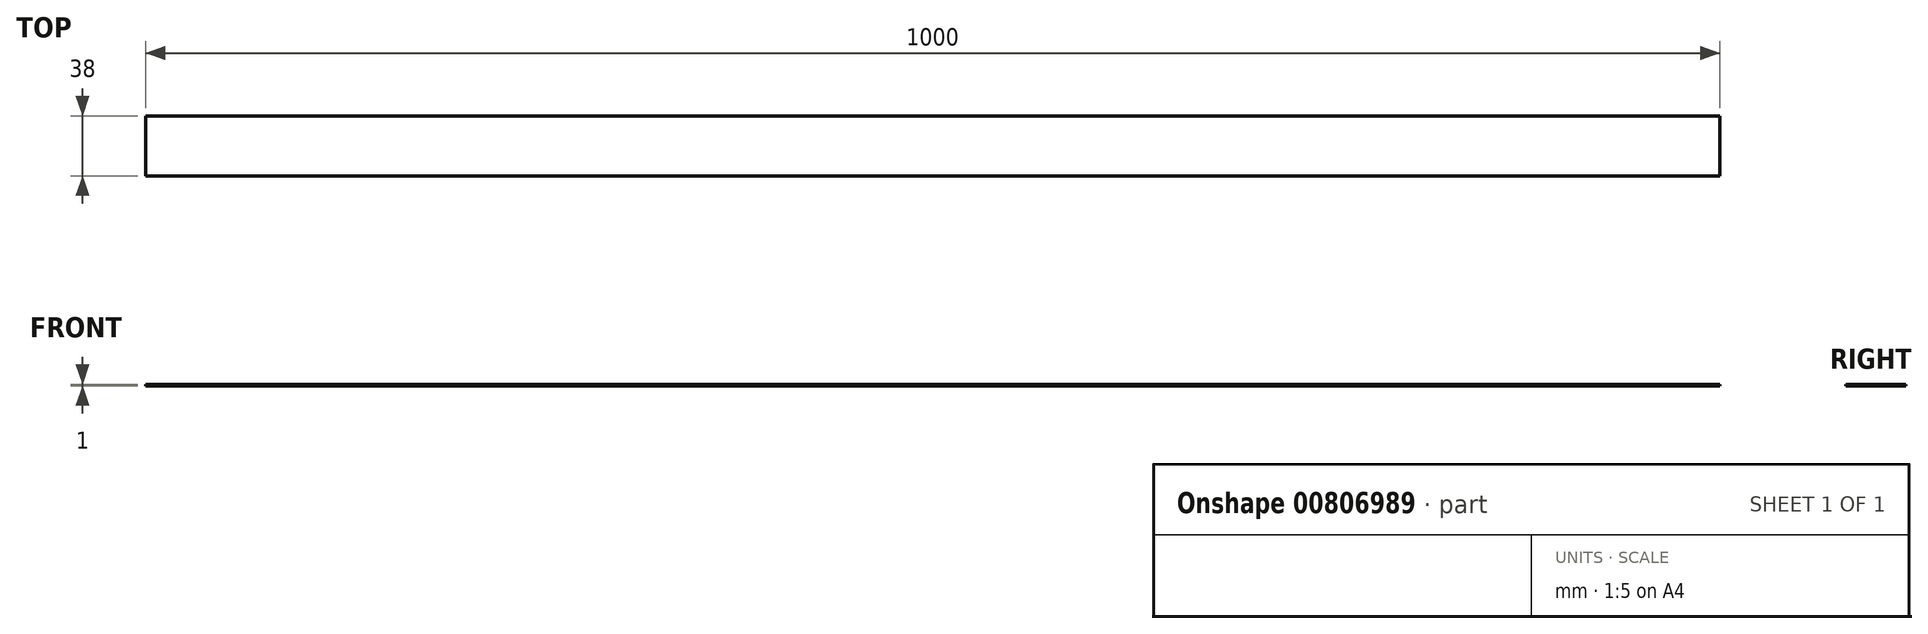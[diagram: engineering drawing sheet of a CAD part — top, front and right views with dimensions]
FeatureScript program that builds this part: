
annotation { "Feature Type Name" : "Feature", "Feature Type Description" : "" }
export const myFeature = defineFeature(function(context is Context, id is Id, definition is map)
    precondition{}
    {
        {
            var Q0;
            Q0=qCreatedBy(makeId("Top.planeOp"),FACE);
            var sketch = newSketch(context, id + "F0", { "sketchPlane" : qUnion([Q0])});
            skLineSegment(sketch, "E0.bottom", {"start": v(-500, 19) * mm, "end": v(500, 19) * mm});
            skLineSegment(sketch, "E0.top", {"start": v(-500, -19) * mm, "end": v(500, -19) * mm});
            skLineSegment(sketch, "E0.left", {"start": v(-500, 19) * mm, "end": v(-500, -19) * mm});
            skLineSegment(sketch, "E0.right", {"start": v(500, 19) * mm, "end": v(500, -19) * mm});
            skSolve(sketch);
        }
        {
            var Q0;
            Q0=makeQuery(id+"F0.imprint","IMPRINT",FACE,{"disambiguationData":[TD([[makeQuery(id+"F0.imprint","IMPRINT",EDGE,{"derivedFrom":sQuery(id+"F0.wireOp",EDGE,"E0.bottom")}),-1.0]])]});
            extrude(context, id + "F1", {"entities" : qUnion([Q0]), "depth" : 1 * mm, "offsetDistance" : 25 * mm});
        }
    });
